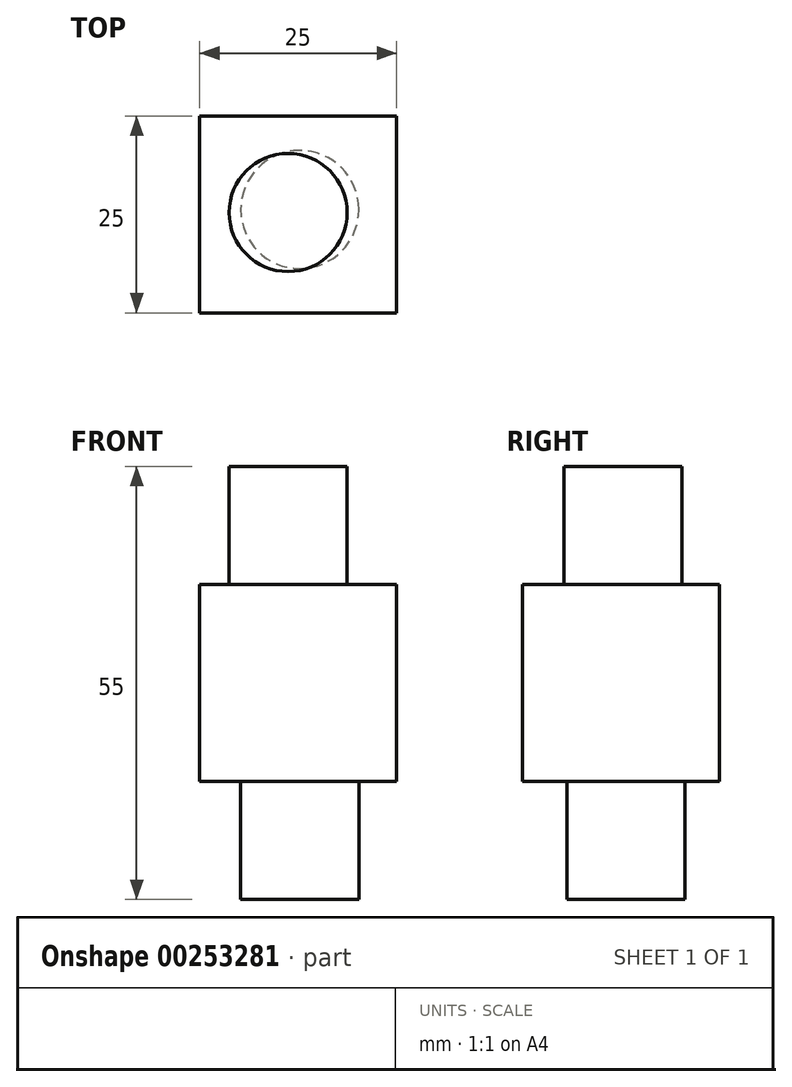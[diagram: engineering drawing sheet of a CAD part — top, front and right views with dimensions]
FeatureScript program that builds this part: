
annotation { "Feature Type Name" : "Feature", "Feature Type Description" : "" }
export const myFeature = defineFeature(function(context is Context, id is Id, definition is map)
    precondition{}
    {
        {
            var Q0;
            Q0=qCreatedBy(makeId("Front.planeOp"),FACE);
            var sketch = newSketch(context, id + "F0", { "sketchPlane" : qUnion([Q0])});
            skLineSegment(sketch, "E0.bottom", {"start": v(0, 0) * mm, "end": v(25, 0) * mm});
            skLineSegment(sketch, "E0.top", {"start": v(0, 25) * mm, "end": v(25, 25) * mm});
            skLineSegment(sketch, "E0.left", {"start": v(0, 0) * mm, "end": v(0, 25) * mm});
            skLineSegment(sketch, "E0.right", {"start": v(25, 0) * mm, "end": v(25, 25) * mm});
            skSolve(sketch);
        }
        {
            var Q0;
            Q0 = qSketchRegion(id + "F0", true);
            extrude(context, id + "F1", {"entities" : qUnion([Q0]), "depth" : 25 * mm});
        }
        {
            var Q0;
            Q0=qCreatedBy(makeId("Top.planeOp"),FACE);
            var sketch = newSketch(context, id + "F2", { "sketchPlane" : qUnion([Q0])});
            skCircle(sketch, "E1", {"center": v(12.7, -11.86) * mm, "radius": 7.5 * mm});
            skSolve(sketch);
        }
        {
            var Q0;
            Q0 = qSketchRegion(id + "F2", true);
            extrude(context, id + "F3", {"entities" : qUnion([Q0]), "operationType" : NewBodyOperationType.ADD, "oppositeDirection" : true, "depth" : 15 * mm});
        }
        {
            var Q0;
            Q0=makeQuery(id+"F1.opExtrude","SWEPT_FACE",FACE,{"disambiguationData":[OSD([sQuery(id+"F0.wireOp",EDGE,"E0.top")])]});
            var sketch = newSketch(context, id + "F4", { "sketchPlane" : qUnion([Q0])});
            skCircle(sketch, "E2", {"center": v(11.22, -12.24) * mm, "radius": 7.5 * mm});
            skSolve(sketch);
        }
        {
            var Q0;
            Q0 = qSketchRegion(id + "F4", true);
            extrude(context, id + "F5", {"entities" : qUnion([Q0]), "operationType" : NewBodyOperationType.ADD, "depth" : 15 * mm});
        }
    });
